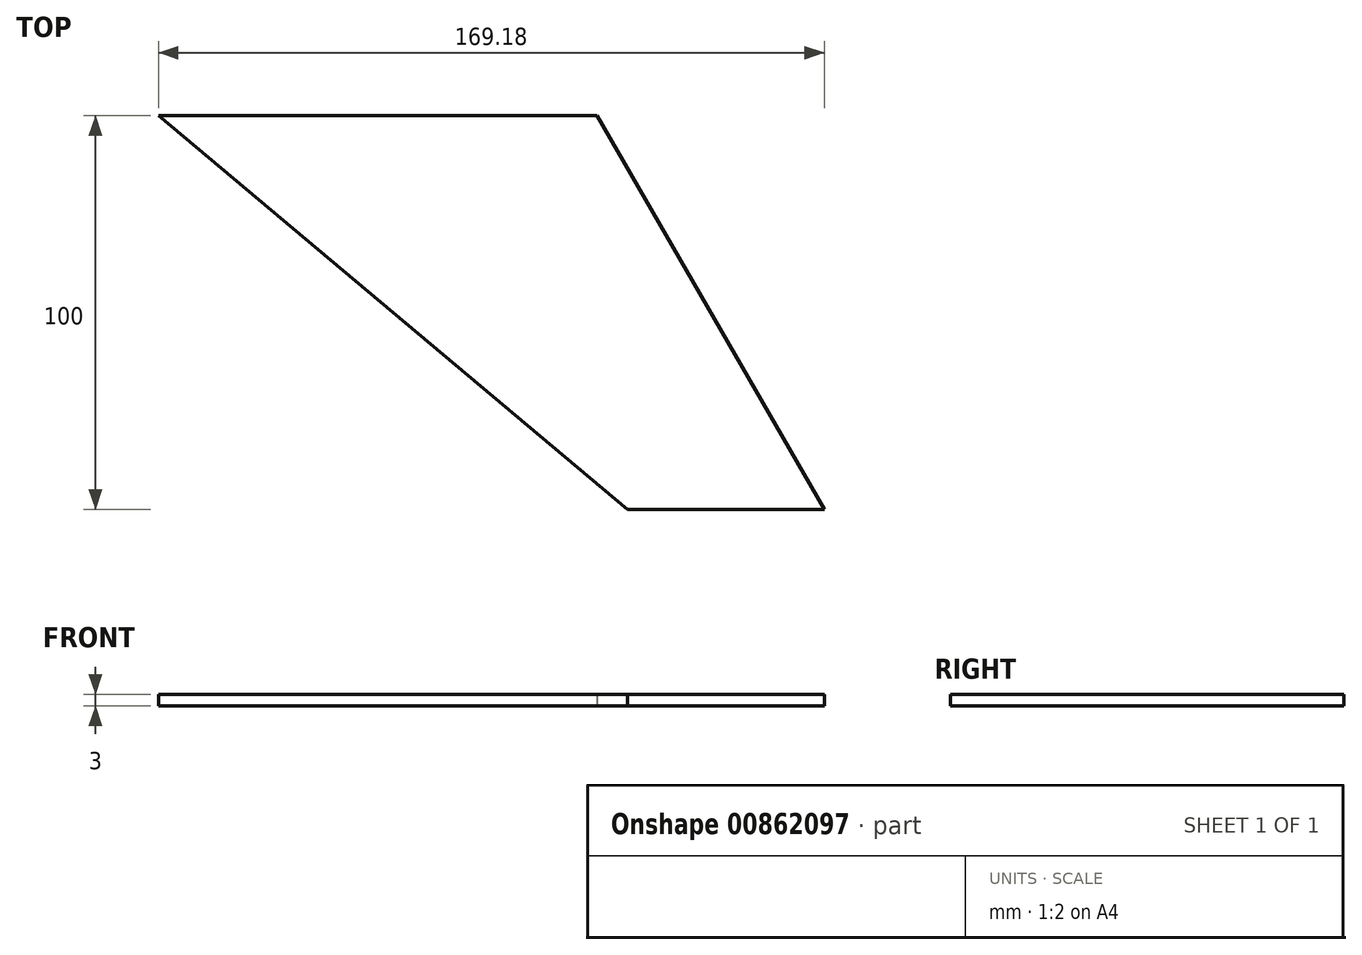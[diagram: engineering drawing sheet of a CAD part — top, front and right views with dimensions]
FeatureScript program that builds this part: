
annotation { "Feature Type Name" : "Feature", "Feature Type Description" : "" }
export const myFeature = defineFeature(function(context is Context, id is Id, definition is map)
    precondition{}
    {
        {
            var Q0;
            Q0=qCreatedBy(makeId("Top.planeOp"),FACE);
            var sketch = newSketch(context, id + "F0", { "sketchPlane" : qUnion([Q0])});
            skLineSegment(sketch, "E0", {"start": v(0, 0) * mm, "end": v(-111.44, 0) * mm});
            skLineSegment(sketch, "E1", {"start": v(-111.44, 0) * mm, "end": v(7.74, -100) * mm});
            skLineSegment(sketch, "E2", {"start": v(7.74, -100) * mm, "end": v(57.74, -100) * mm});
            skLineSegment(sketch, "E3", {"start": v(57.74, -100) * mm, "end": v(0, 0) * mm});
            skSolve(sketch);
        }
        {
            var Q0;
            Q0=makeQuery(id+"F0.imprint","IMPRINT",FACE,{"disambiguationData":[TD([[makeQuery(id+"F0.imprint","IMPRINT",EDGE,{"derivedFrom":sQuery(id+"F0.wireOp",EDGE,"E0")}),1.0]])]});
            extrude(context, id + "F1", {"entities" : qUnion([Q0]), "depth" : 3 * mm, "offsetDistance" : 25 * mm});
        }
    });
